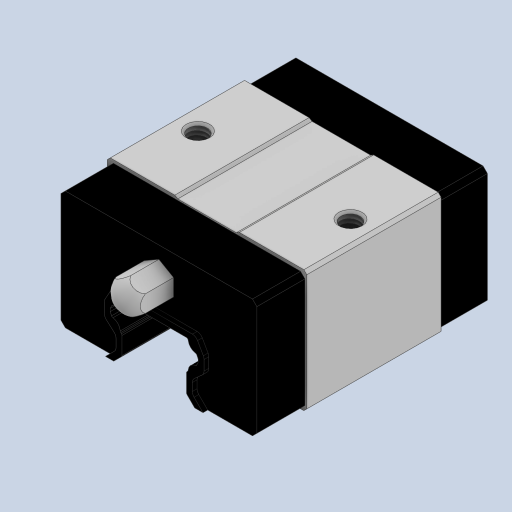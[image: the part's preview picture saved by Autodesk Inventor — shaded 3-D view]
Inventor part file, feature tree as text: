
AUTODESK INVENTOR PART (.ipt)
format: ipt  version: 2023 (Build 270158000, 158)  size: 608,768 bytes
history: native  units: mm
features: sketch x13, extrude x10, other x7, hole x2, revolve x1
ambient origin geometry x8: Origin, YZ Plane, XZ Plane, XY Plane, X Axis, Y Axis, Z Axis, Center Point
bodies: Solid1 (feature_tree)
feature tree (33):
  extrude  "Extrusion1"  Depth=39.3mm TaperAngle=0.0deg
  extrude  "Extrusion2"  Depth=7.0mm TaperAngle=0.0deg
  revolve  "Revolution1"  [1 undecoded]
  extrude  "Extrusion3"  Depth=11.45mm TaperAngle=0.0deg
  extrude  "Extrusion4"  Depth=0.05mm TaperAngle=0.0deg
  extrude  "Extrusion5"  [1 undecoded]
  extrude  "Extrusion6"  [1 undecoded]
  extrude  "Extrusion7"  [1 undecoded]
  extrude  "Extrusion8"  [1 undecoded]
  hole  "Hole1"  [1 undecoded]
  hole  "Hole2"  [1 undecoded]
  extrude  "Extrusion9"  [1 undecoded]
  extrude  "Extrusion10"  [1 undecoded]
  other  "to_rail_XY"
  other  "to_rail_YZ"
  other  "to_rail_ZX"
  other  "to_rail_X"
  other  "to_rail_Y"
  other  "to_rail_Z"
  other  "to_rail_Center"
  sketch  "Sketch_1"  dims[d0=22.9mm d1=0.0mm d2=39.3mm d3=0.0mm]
  sketch  "Sketch_2"  dims[d4=360.0deg d5=7.0mm d6=0.0mm]
  sketch  "Sketch_32"
  sketch  "Sketch_33"
  sketch  "Sketch_7"  dims[d11=22.9mm d12=0.0mm d13=11.45mm d14=0.0mm]
  sketch  "Sketch_10"  dims[d15=11.45mm d16=0.0mm]
  sketch  "Sketch_3"  dims[d7=0.8mm d8=0.0mm d9=0.8mm d10=0.0mm]
  sketch  "Sketch_11"  dims[d24=3.242mm d25=5.0mm d26=4.0mm d27=2.0mm d28=90.0deg d29=7.1mm d30=120.0deg d31=0.05mm d32=0.0mm]
  sketch  "Sketch_12"
  sketch  "Sketch10"  dims[d17=3.242mm d18=5.0mm d19=4.0mm d20=2.0mm d21=90.0deg d22=7.1mm d23=120.0deg]
  sketch  "Sketch11"  dims[d33=0.05mm d34=0.0mm]
  sketch  "Sketch_29"
  sketch  "Sketch_30"
note: 9 required parameter values undecoded (feature->parameter linkage not recoverable at this tier; creation-order binding heuristic only, values carry confidence <= 0.55)